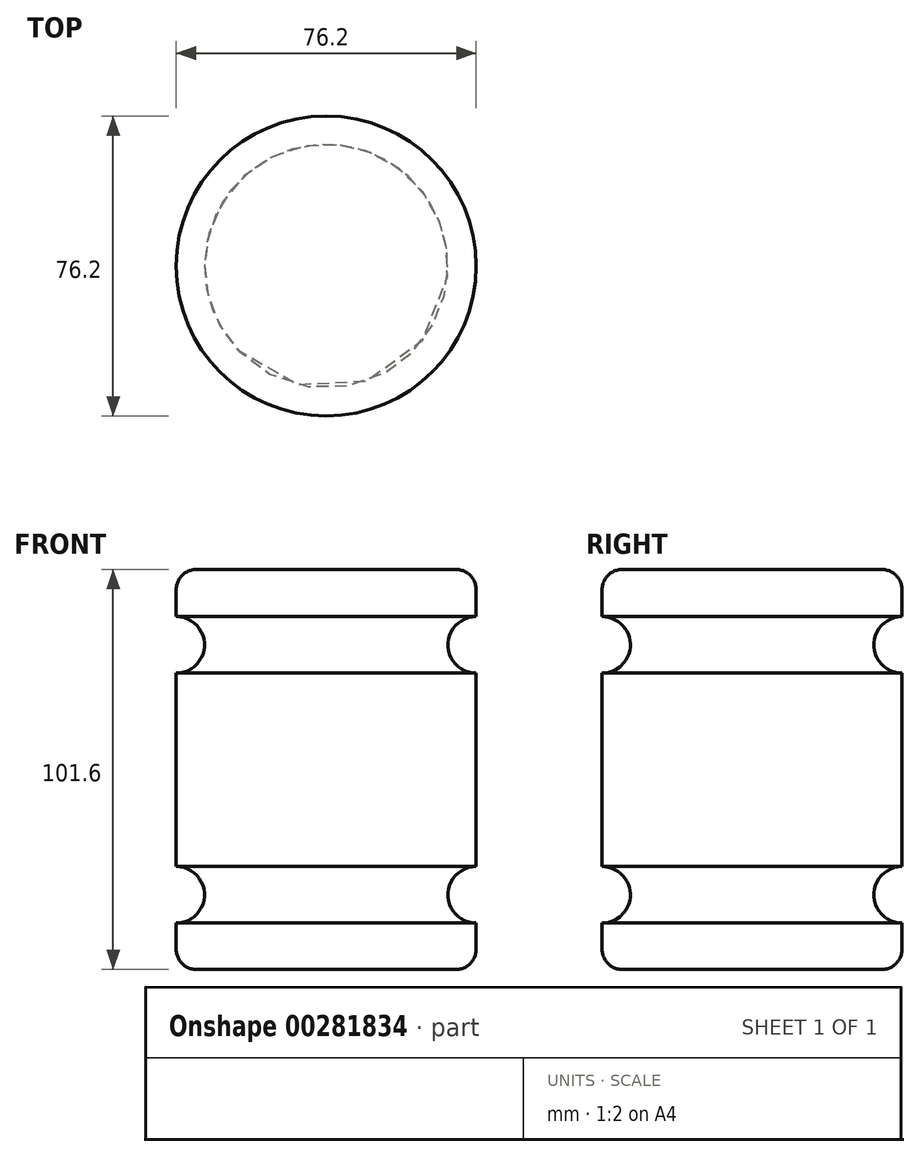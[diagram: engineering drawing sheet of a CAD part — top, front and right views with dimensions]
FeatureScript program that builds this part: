
annotation { "Feature Type Name" : "Feature", "Feature Type Description" : "" }
export const myFeature = defineFeature(function(context is Context, id is Id, definition is map)
    precondition{}
    {
        {
            var Q0;
            Q0=qCreatedBy(makeId("Front.planeOp"),FACE);
            var sketch = newSketch(context, id + "F0", { "sketchPlane" : qUnion([Q0])});
            skLineSegment(sketch, "E0", {"start": v(0, 0) * mm, "end": v(0, 11.78) * mm});
            skLineSegment(sketch, "E1", {"start": v(0, 0) * mm, "end": v(-38.1, 0) * mm});
            skLineSegment(sketch, "E2", {"start": v(-38.1, 0) * mm, "end": v(-38.1, 101.6) * mm});
            skLineSegment(sketch, "E3", {"start": v(-38.1, 101.6) * mm, "end": v(0, 101.6) * mm});
            skArc(sketch, "E4", {"start": v(0, 89.64) * mm, "mid": v(-7.18, 82.46) * mm, "end": v(0, 75.27) * mm});
            skArc(sketch, "E5", {"start": v(0, 26.13) * mm, "mid": v(-7.18, 18.95) * mm, "end": v(0, 11.78) * mm});
            skLineSegment(sketch, "E6.trimOffspring", {"start": v(0, 26.13) * mm, "end": v(0, 75.27) * mm});
            skLineSegment(sketch, "E7.trimOffspring", {"start": v(0, 89.64) * mm, "end": v(0, 101.6) * mm});
            skSolve(sketch);
        }
        {
            var Q0;
            Q0=makeQuery(id+"F0.imprint","IMPRINT",FACE,{"disambiguationData":[TD([[makeQuery(id+"F0.imprint","IMPRINT",EDGE,{"derivedFrom":sQuery(id+"F0.wireOp",EDGE,"E0")}),1.0]])]});
            var Q1;
            Q1=sQuery(id+"F0.wireOp",EDGE,"E2");
            revolve(context, id + "F1", {"entities" : qUnion([Q0]), "axis" : qUnion([Q1]), "revolveType" : RevolveType.FULL});
        }
        {
            var Q0;
            Q0=makeQuery(id+"F1.opRevolve","SWEPT_EDGE",EDGE,{"disambiguationData":[OSD([sQuery(id+"F0.wireOp",EDGE,"E3"),sQuery(id+"F0.wireOp",EDGE,"E7.trimOffspring")])]});
            var Q1;
            Q1=makeQuery(id+"F1.opRevolve","SWEPT_EDGE",EDGE,{"disambiguationData":[OSD([sQuery(id+"F0.wireOp",EDGE,"E0"),sQuery(id+"F0.wireOp",EDGE,"E1")])]});
            fillet(context, id + "F2", {"entities" : qUnion([Q0, Q1]), "radius" : 5.08 * mm, "tangentPropagation" : true, "allowEdgeOverflow" : false});
        }
    });
